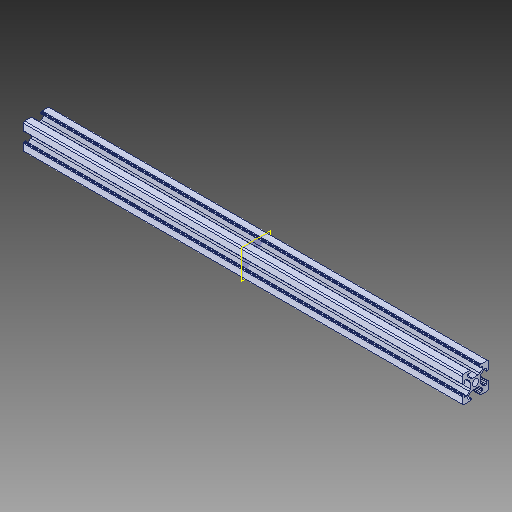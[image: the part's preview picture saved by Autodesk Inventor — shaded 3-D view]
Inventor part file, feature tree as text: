
AUTODESK INVENTOR PART (.ipt)
format: ipt  version: 2018 (Build 220112000, 112)  size: 371,200 bytes
history: native  units: in
note: dims shown in document units (in); Inventor stores cm internally (conversion verified against a paired STEP export)
features: extrude x1, plane x1, sketch x1, projected_geometry x1, fillet x1
ambient origin geometry x8: Origin, YZ Plane, XZ Plane, XY Plane, X Axis, Y Axis, Z Axis, Center Point
bodies: Solid1 (feature_tree)
feature tree (5):
  extrude  "Extrusion2"  [1 undecoded]
  plane  "Work Plane1"
  sketch  "Sketch3"  dims[d2=9.0551in d3=0.0in]
  projected_geometry  "Projected Loop2"
  fillet  "Fillet5"  [1 undecoded]
note: 2 required parameter values undecoded (feature->parameter linkage not recoverable at this tier; creation-order binding heuristic only, values carry confidence <= 0.55)
